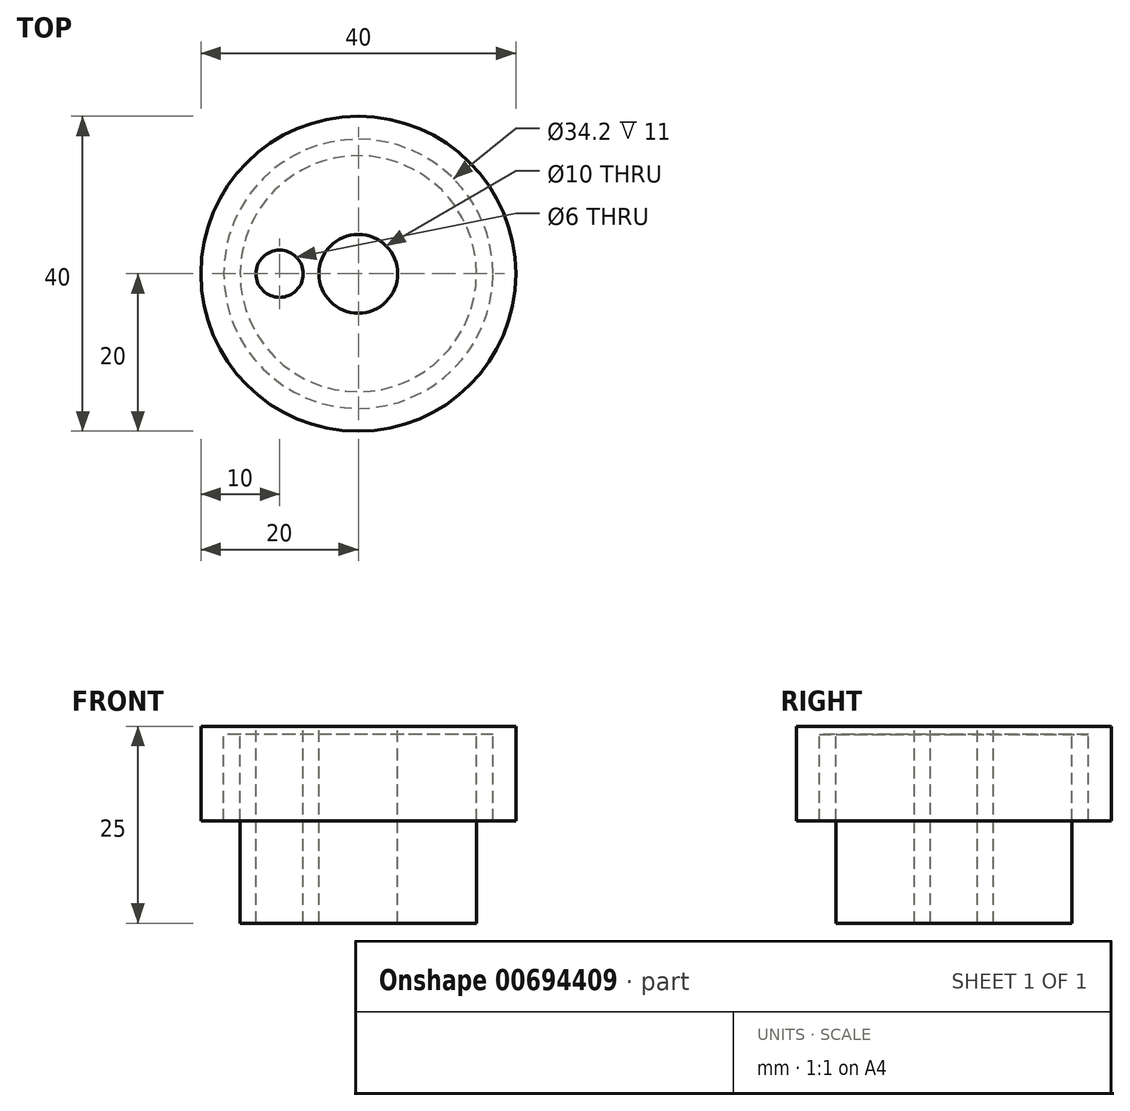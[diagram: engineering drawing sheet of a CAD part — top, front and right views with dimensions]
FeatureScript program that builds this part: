
annotation { "Feature Type Name" : "Feature", "Feature Type Description" : "" }
export const myFeature = defineFeature(function(context is Context, id is Id, definition is map)
    precondition{}
    {
        {
            var Q0;
            Q0=qCreatedBy(makeId("Front.planeOp"),FACE);
            var sketch = newSketch(context, id + "F0", { "sketchPlane" : qUnion([Q0])});
            skLineSegment(sketch, "E0", {"start": v(0, 0) * mm, "end": v(20, 0) * mm});
            skLineSegment(sketch, "E1", {"start": v(20, 0) * mm, "end": v(20, -12) * mm});
            skLineSegment(sketch, "E2", {"start": v(20, -12) * mm, "end": v(17.1, -12) * mm});
            skLineSegment(sketch, "E3", {"start": v(17.1, -12) * mm, "end": v(17.1, -1) * mm});
            skLineSegment(sketch, "E4", {"start": v(17.1, -1) * mm, "end": v(15, -1) * mm});
            skLineSegment(sketch, "E5", {"start": v(15, -1) * mm, "end": v(15, -25) * mm});
            skLineSegment(sketch, "E6", {"start": v(15, -25) * mm, "end": v(0, -25) * mm});
            skLineSegment(sketch, "E7", {"start": v(0, -25) * mm, "end": v(0, 0) * mm});
            skLineSegment(sketch, "E8", {"start": v(0, 12.07) * mm, "end": v(0, -53.6) * mm, "construction": true});
            skSolve(sketch);
        }
        {
            var Q0;
            Q0=makeQuery(id+"F0.imprint","IMPRINT",FACE,{"disambiguationData":[TD([[makeQuery(id+"F0.imprint","IMPRINT",EDGE,{"derivedFrom":sQuery(id+"F0.wireOp",EDGE,"E0")}),-1.0]])]});
            var Q1;
            Q1=sQuery(id+"F0.wireOp",EDGE,"E8");
            revolve(context, id + "F1", {"entities" : qUnion([Q0]), "axis" : qUnion([Q1]), "revolveType" : RevolveType.FULL});
        }
        {
            var Q0;
            Q0=qCreatedBy(makeId("Top.planeOp"),FACE);
            var sketch = newSketch(context, id + "F2", { "sketchPlane" : qUnion([Q0])});
            skCircle(sketch, "E9", {"center": v(0, 0) * mm, "radius": 5 * mm});
            skSolve(sketch);
        }
        {
            var Q0;
            Q0 = qSketchRegion(id + "F2", true);
            extrude(context, id + "F3", {"entities" : qUnion([Q0]), "operationType" : NewBodyOperationType.REMOVE, "endBound" : BoundingType.THROUGH_ALL, "oppositeDirection" : true, "depth" : 25 * mm, "offsetDistance" : 25 * mm});
        }
        {
            var Q0;
            Q0=makeQuery(id+"F1.opRevolve","SWEPT_FACE",FACE,{"disambiguationData":[OSD([sQuery(id+"F0.wireOp",EDGE,"E0")])]});
            var sketch = newSketch(context, id + "F4", { "sketchPlane" : qUnion([Q0])});
            skCircle(sketch, "E10", {"center": v(-10, 0) * mm, "radius": 3 * mm});
            skSolve(sketch);
        }
        {
            var Q0;
            Q0=makeQuery(id+"F4.imprint","IMPRINT",FACE,{"disambiguationData":[TD([[makeQuery(id+"F4.imprint","IMPRINT",EDGE,{"derivedFrom":sQuery(id+"F4.wireOp",EDGE,"E10")}),1.0]])]});
            extrude(context, id + "F5", {"entities" : qUnion([Q0]), "operationType" : NewBodyOperationType.REMOVE, "endBound" : BoundingType.THROUGH_ALL, "oppositeDirection" : true, "depth" : 25 * mm, "offsetDistance" : 25 * mm});
        }
    });
